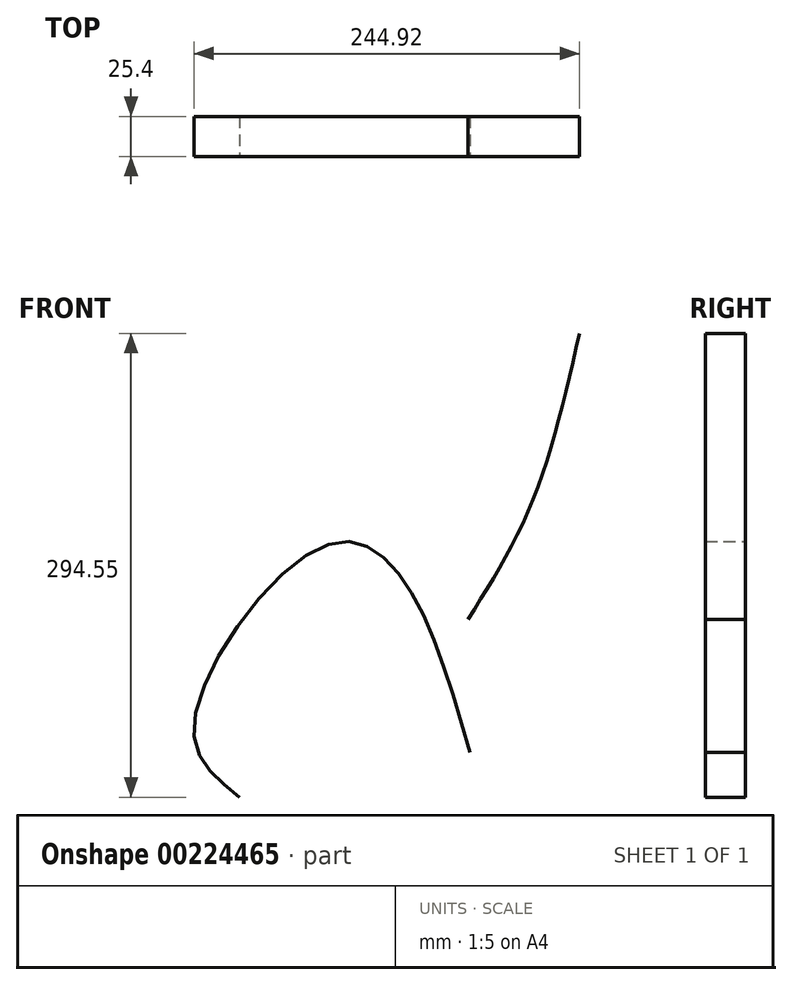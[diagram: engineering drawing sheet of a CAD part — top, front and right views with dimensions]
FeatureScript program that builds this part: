
annotation { "Feature Type Name" : "Feature", "Feature Type Description" : "" }
export const myFeature = defineFeature(function(context is Context, id is Id, definition is map)
    precondition{}
    {
        {
            var Q0;
            Q0=qCreatedBy(makeId("Front.planeOp"),FACE);
            var sketch = newSketch(context, id + "F0", { "sketchPlane" : qUnion([Q0])});
            skFitSpline(sketch, "E0", {"points": [v(100.38, 166.32) * mm, v(69.81, 58.25) * mm, v(29.43, -15.46) * mm], "startDerivative": vector(-48.96, -212.99) * mm, "endDerivative": vector(-94.03, -149.03) * mm});
            skFitSpline(sketch, "E1", {"points": [v(-115.44, -128.23) * mm, v(-144.41, -81.84) * mm, v(-61.6, 31.5) * mm, v(-11.86, 10.04) * mm, v(30.8, -99.93) * mm], "startDerivative": vector(-233.04, 180.43) * mm, "endDerivative": vector(123.03, -430.1) * mm});
            skSolve(sketch);
        }
        {
            var Q0;
            Q0=sQuery(id+"F0.wireOp",EDGE,"E0");
            var Q1;
            Q1=sQuery(id+"F0.wireOp",EDGE,"E1");
            extrude(context, id + "F1", {"bodyType" : ToolBodyType.SURFACE, "surfaceEntities" : qUnion([Q0, Q1]), "depth" : 25.4 * mm});
        }
    });
